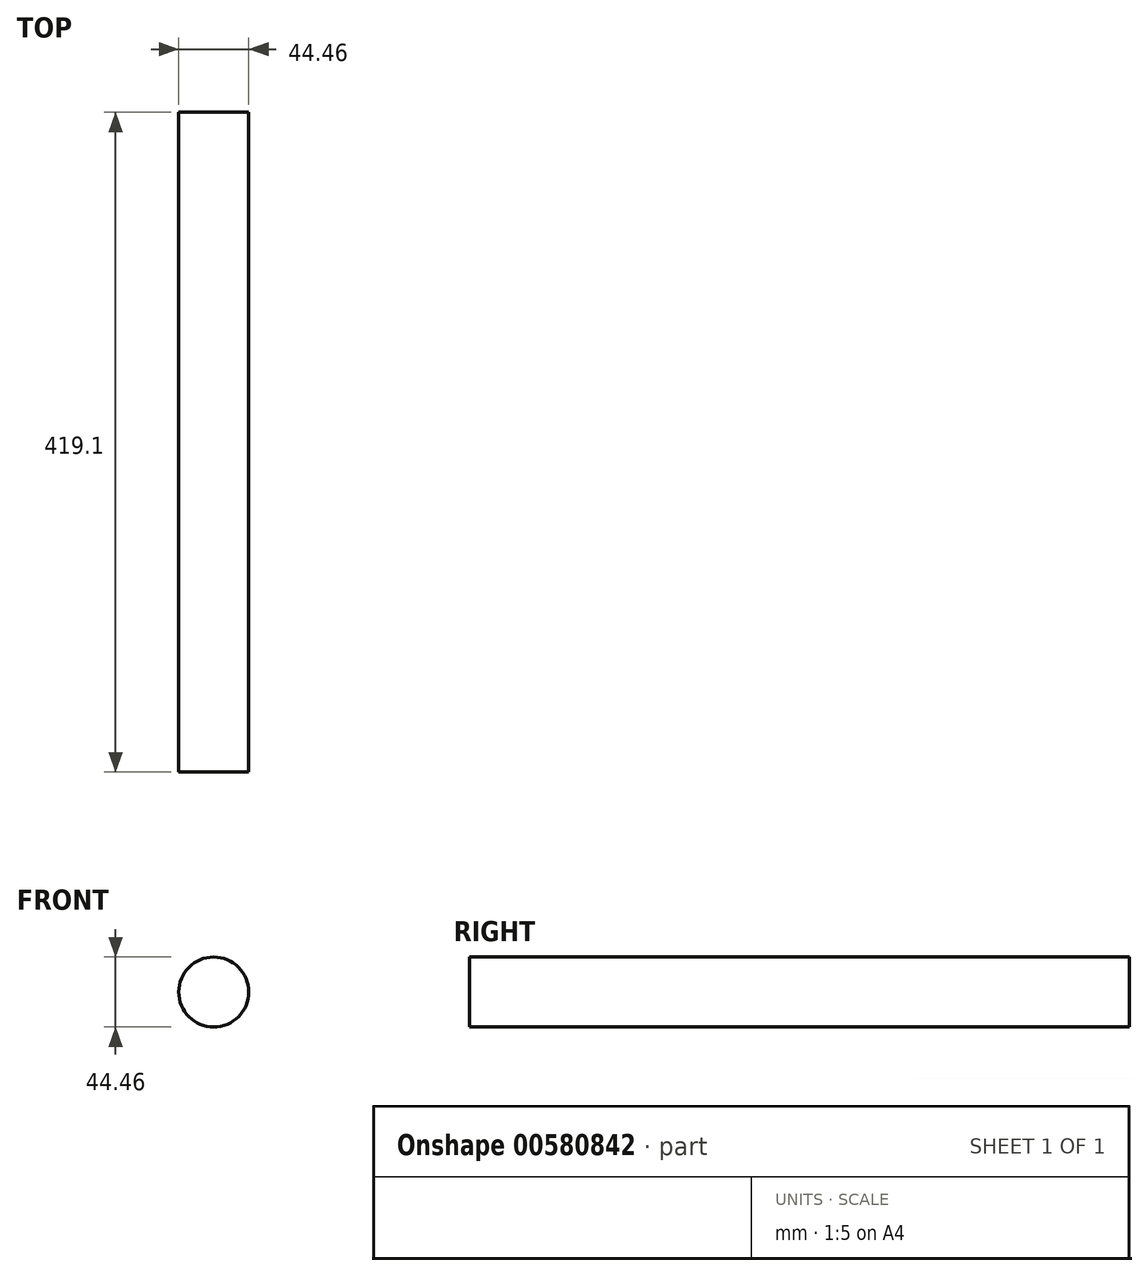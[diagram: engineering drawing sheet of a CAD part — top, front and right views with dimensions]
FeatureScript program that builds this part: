
annotation { "Feature Type Name" : "Feature", "Feature Type Description" : "" }
export const myFeature = defineFeature(function(context is Context, id is Id, definition is map)
    precondition{}
    {
        {
            var Q0;
            Q0=qCreatedBy(makeId("Front.planeOp"),FACE);
            var sketch = newSketch(context, id + "F0", { "sketchPlane" : qUnion([Q0])});
            skCircle(sketch, "E0", {"center": v(0, 0) * mm, "radius": 22.23 * mm});
            skSolve(sketch);
        }
        {
            var Q0;
            Q0 = qSketchRegion(id + "F0", true);
            extrude(context, id + "F1", {"entities" : qUnion([Q0]), "depth" : 419.1 * mm, "offsetDistance" : 25.4 * mm});
        }
    });
